# Revit family: FantiniCosmi_BIM_AP3104
name_source: partatom
category: Generic Models
units: mm (PartAtom-declared; Revit-internal decimal feet)

## family parameters
Always vertical = Yes
Can host rebar = No
Cut with Voids When Loaded = No
Part Type = Normal
Room Calculation Point = No
Round Connector Dimension = Use Diameter
Shared = No
Work Plane-Based = No

## types (1)
- Standard
    Air flow = 55 m³/h
    Catalog web link = https://www.fantinicosmi.it
    Comments = The fan automatically starts to operate when the relative humidity level in the room exceeds the pre-set value and it continues to
operate until the RH level returns below the preset threshold. When this threshold is reached, TIMER function allows the extractor
fan to continue working for a period of time that can be set from about 45 seconds to 20 minutes, to further reduce relative humidity
in the room. The relative humidity value can be set from a minimum of 40% RH to a maximum of 80% RH. This extractor fan can be
used manually, also using the TIMER function.
    Current = 0.1 A
    Default Elevation = 0 mm  [stored 0 ft]
    Description = Axial fan with high performance
    Designer = Carniti
    Ducting Ø = 120 mm / 5”
    Frequency = 50 Hz
    Humidity protection = IPX4
    Model = Aspirante (120)
    Part Number = AP3104 (Ø120mm)
    Power = 24 W
    Pt max = 9 mmH2O
    Sound Pressure 3Mt = 43 dB(A)
    Voltage = 230 V
    Weight = 0.7 Kg

note: [stored X ft] marks values corroborated as IEEE doubles in the binary element streams (Revit-internal decimal feet)

## geometry (parser evidence)
native form markers: Sweep x2
no freeform markers — native parametric forms only
